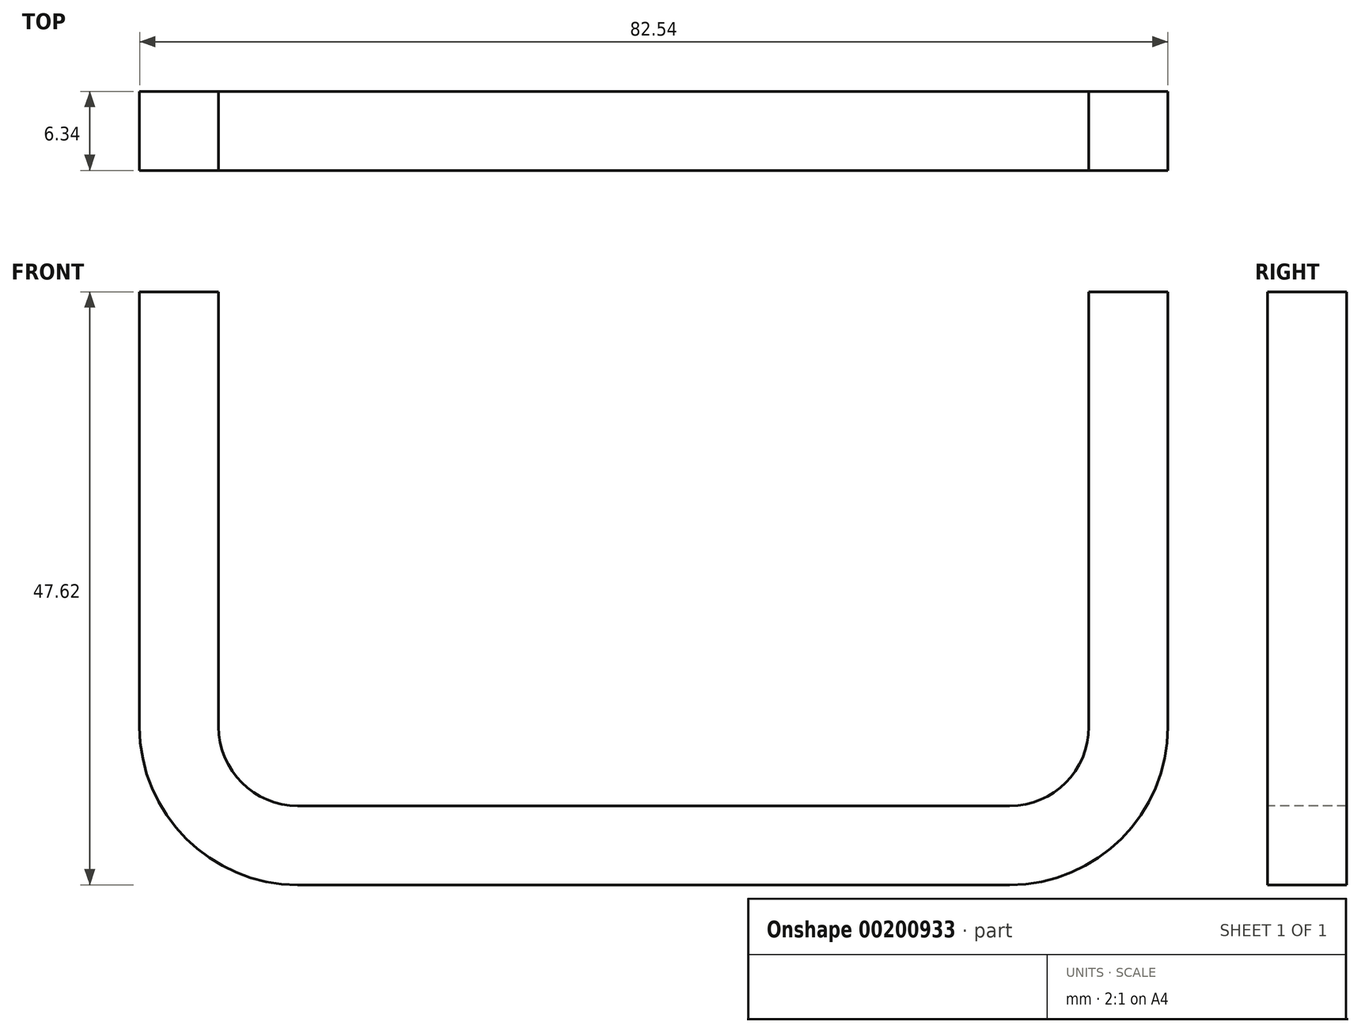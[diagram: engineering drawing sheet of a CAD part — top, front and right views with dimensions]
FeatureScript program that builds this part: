
annotation { "Feature Type Name" : "Feature", "Feature Type Description" : "" }
export const myFeature = defineFeature(function(context is Context, id is Id, definition is map)
    precondition{}
    {
        {
            var Q0;
            Q0=qCreatedBy(makeId("Front.planeOp"),FACE);
            var sketch = newSketch(context, id + "F0", { "sketchPlane" : qUnion([Q0])});
            skLineSegment(sketch, "E0", {"start": v(0, 0) * mm, "end": v(28.58, 0) * mm});
            skLineSegment(sketch, "E1", {"start": v(0, 0) * mm, "end": v(-28.58, 0) * mm});
            skLineSegment(sketch, "E2", {"start": v(-38.1, 9.52) * mm, "end": v(-38.1, 44.45) * mm});
            skLineSegment(sketch, "E3", {"start": v(38.1, 9.53) * mm, "end": v(38.1, 44.45) * mm});
            skPoint(sketch, "E4.visualSharp", {"position": v(-38.1, 0) * mm});
            skArc(sketch, "E4.filletArc", {"start": v(-38.1, 9.52) * mm, "mid": v(-35.31, 2.79) * mm, "end": v(-28.58, 0) * mm});
            skPoint(sketch, "E5.visualSharp", {"position": v(38.1, 0) * mm});
            skArc(sketch, "E5.filletArc", {"start": v(28.58, 0) * mm, "mid": v(35.31, 2.79) * mm, "end": v(38.1, 9.53) * mm});
            skSolve(sketch);
        }
        {
            var Q0;
            Q0=qCreatedBy(makeId("Top.planeOp"),FACE);
            cPlane(context, id + "F1", {"entities" : qUnion([Q0]), "cplaneType" : CPlaneType.OFFSET, "offset" : 44.45 * mm, "width" : 152.4 * mm, "height" : 152.4 * mm});
        }
        {
            var Q0;
            Q0=qCreatedBy(id+"F1.planeOp",FACE);
            var sketch = newSketch(context, id + "F2", { "sketchPlane" : qUnion([Q0])});
            skPoint(sketch, "E6.middle", {"position": v(-38.1, 0) * mm});
            skLineSegment(sketch, "E7.bottom", {"start": v(-34.93, 3.17) * mm, "end": v(-41.28, 3.17) * mm});
            skLineSegment(sketch, "E7.top", {"start": v(-34.93, -3.18) * mm, "end": v(-41.28, -3.18) * mm});
            skLineSegment(sketch, "E7.left", {"start": v(-34.93, 3.17) * mm, "end": v(-34.93, -3.18) * mm});
            skLineSegment(sketch, "E7.right", {"start": v(-41.28, 3.17) * mm, "end": v(-41.28, -3.18) * mm});
            skSolve(sketch);
        }
        {
            var Q0;
            Q0=makeQuery(id+"F2.imprint","IMPRINT",FACE,{"disambiguationData":[TD([[makeQuery(id+"F2.imprint","IMPRINT",EDGE,{"derivedFrom":sQuery(id+"F2.wireOp",EDGE,"E7.bottom")}),1.0]])]});
            var Q1;
            Q1 = qConstructionFilter(qBodyType(qCreatedBy(id + "F0" ,EDGE), BodyType.WIRE), ConstructionObject.NO);
            sweep(context, id + "F3", {"profiles" : qUnion([Q0]), "path" : qUnion([Q1])});
        }
    });
